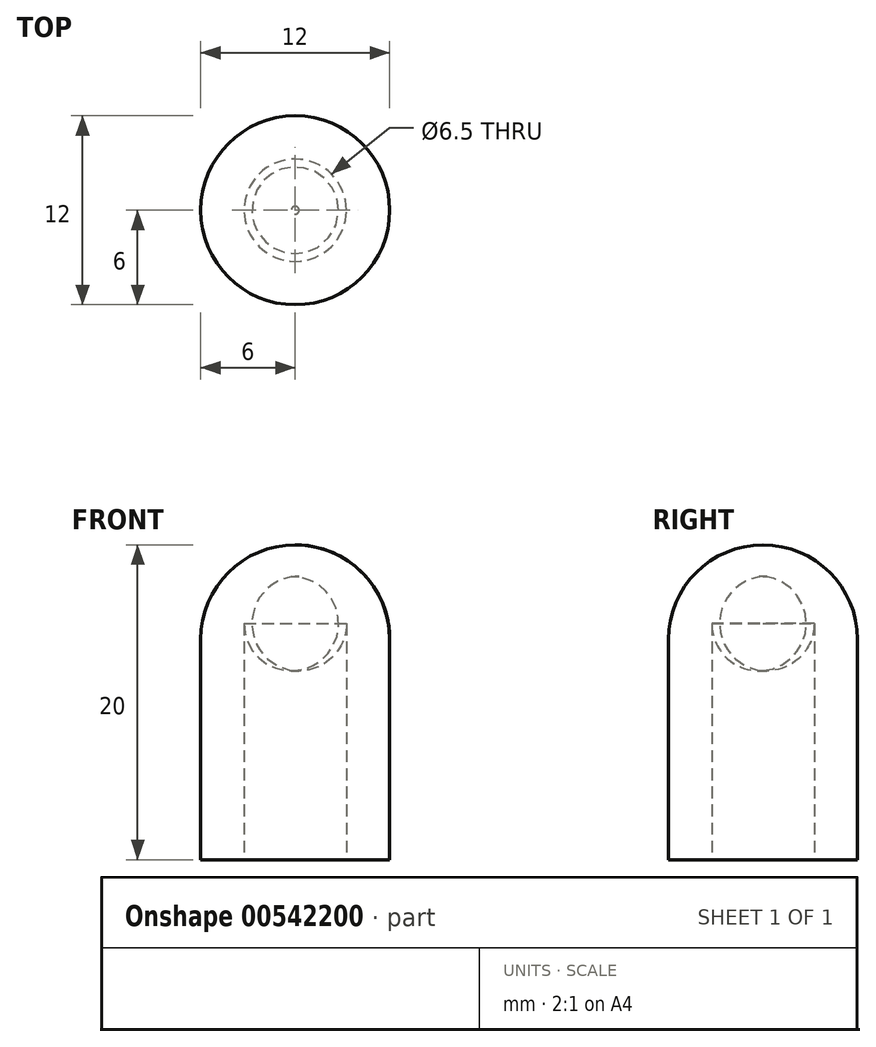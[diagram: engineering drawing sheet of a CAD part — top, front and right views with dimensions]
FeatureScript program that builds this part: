
annotation { "Feature Type Name" : "Feature", "Feature Type Description" : "" }
export const myFeature = defineFeature(function(context is Context, id is Id, definition is map)
    precondition{}
    {
        {
            var Q0;
            Q0=qCreatedBy(makeId("Top.planeOp"),FACE);
            var sketch = newSketch(context, id + "F0", { "sketchPlane" : qUnion([Q0])});
            skCircle(sketch, "E0", {"center": v(0, 0) * mm, "radius": 6 * mm});
            skSolve(sketch);
        }
        {
            var Q0;
            Q0=makeQuery(id+"F0.imprint","IMPRINT",FACE,{"disambiguationData":[TD([[makeQuery(id+"F0.imprint","IMPRINT",EDGE,{"derivedFrom":sQuery(id+"F0.wireOp",EDGE,"E0")}),1.0]])]});
            extrude(context, id + "F1", {"entities" : qUnion([Q0]), "depth" : 20 * mm, "offsetDistance" : 25 * mm});
        }
        {
            var Q0;
            Q0=makeQuery(id+"F1.opExtrude","CAP_EDGE",EDGE,{"disambiguationData":[OSD([sQuery(id+"F0.wireOp",EDGE,"E0")])],"isStart":false});
            fillet(context, id + "F2", {"entities" : qUnion([Q0]), "radius" : 6 * mm, "tangentPropagation" : true, "allowEdgeOverflow" : false});
        }
        {
            var Q0;
            Q0=makeQuery(id+"F1.opExtrude","CAP_FACE",FACE,{"disambiguationData":[OSD([sQuery(id+"F0.wireOp",EDGE,"E0")])],"isStart":true});
            var sketch = newSketch(context, id + "F3", { "sketchPlane" : qUnion([Q0])});
            skCircle(sketch, "E1", {"center": v(0, 0) * mm, "radius": 3.25 * mm});
            skSolve(sketch);
        }
        {
            var Q0;
            Q0=makeQuery(id+"F3.imprint","IMPRINT",FACE,{"disambiguationData":[TD([[makeQuery(id+"F3.imprint","IMPRINT",EDGE,{"derivedFrom":sQuery(id+"F3.wireOp",EDGE,"E1")}),1.0]])]});
            extrude(context, id + "F4", {"entities" : qUnion([Q0]), "operationType" : NewBodyOperationType.REMOVE, "oppositeDirection" : true, "depth" : 18 * mm, "offsetDistance" : 25 * mm});
        }
        {
            var Q0;
            Q0=makeQuery(id+"F4.boolean.opBoolean","COPY",EDGE,{"derivedFrom":makeQuery(id+"F4.opExtrude","CAP_EDGE",EDGE,{"disambiguationData":[OSD([sQuery(id+"F3.wireOp",EDGE,"E1")])],"isStart":false})});
            fillet(context, id + "F5", {"entities" : qUnion([Q0]), "radius" : 3 * mm, "tangentPropagation" : true, "allowEdgeOverflow" : false});
        }
    });
